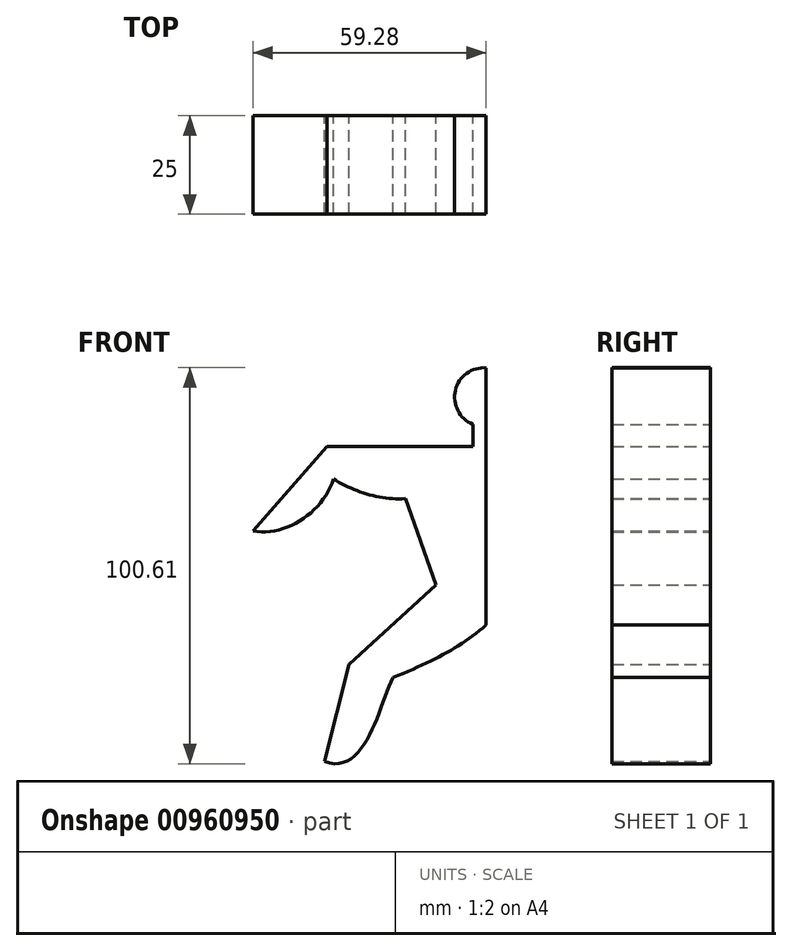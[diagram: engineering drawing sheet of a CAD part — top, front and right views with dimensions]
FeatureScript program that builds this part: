
annotation { "Feature Type Name" : "Feature", "Feature Type Description" : "" }
export const myFeature = defineFeature(function(context is Context, id is Id, definition is map)
    precondition{}
    {
        {
            var Q0;
            Q0=qCreatedBy(makeId("Front.planeOp"),FACE);
            var sketch = newSketch(context, id + "F0", { "sketchPlane" : qUnion([Q0])});
            skLineSegment(sketch, "E0", {"start": v(-3.4, 30.59) * mm, "end": v(-3.4, 24.97) * mm});
            skLineSegment(sketch, "E1", {"start": v(-3.4, 24.97) * mm, "end": v(-40.44, 24.97) * mm});
            skLineSegment(sketch, "E2", {"start": v(-40.44, 24.97) * mm, "end": v(-59.28, 3.51) * mm});
            skLineSegment(sketch, "E3", {"start": v(-20.5, 11.74) * mm, "end": v(-12.75, -10.25) * mm});
            skLineSegment(sketch, "E4", {"start": v(-12.75, -10.25) * mm, "end": v(-34.88, -30.44) * mm});
            skLineSegment(sketch, "E5", {"start": v(-34.88, -30.44) * mm, "end": v(-41.13, -55.05) * mm});
            skFitSpline(sketch, "E6", {"points": [v(-59.28, 3.51) * mm, v(-38.82, 16.7) * mm], "startDerivative": vector(24.73, -5.03) * mm, "endDerivative": vector(7.62, 25.02) * mm});
            skFitSpline(sketch, "E7", {"points": [v(-38.82, 16.7) * mm, v(-20.5, 11.74) * mm], "startDerivative": vector(16.19, -9.8) * mm, "endDerivative": vector(19.1, 1.69) * mm});
            skFitSpline(sketch, "E8", {"points": [v(-41.13, -55.05) * mm, v(-23.7, -33.74) * mm], "startDerivative": vector(31.12, -11.97) * mm, "endDerivative": vector(11.29, 24.28) * mm});
            skPoint(sketch, "E9.1.internal.snap0", {"position": v(-23.81, -20.35) * mm});
            skFitSpline(sketch, "E9", {"points": [v(-23.7, -33.74) * mm, v(0, -20.35) * mm], "startDerivative": vector(31.12, 12.31) * mm, "endDerivative": vector(20.12, 17.26) * mm});
            skArc(sketch, "E10", {"start": v(0, 44.95) * mm, "mid": v(-7.83, 39.22) * mm, "end": v(-3.4, 30.59) * mm});
            skLineSegment(sketch, "E11", {"start": v(0, 44.95) * mm, "end": v(0, -21.96) * mm, "construction": true});
            skLineSegment(sketch, "E12.MirrorCS", {"start": v(20.5, 11.74) * mm, "end": v(12.75, -10.25) * mm});
            skLineSegment(sketch, "E13.MirrorCS", {"start": v(34.88, -30.44) * mm, "end": v(41.13, -55.05) * mm});
            skLineSegment(sketch, "E14.MirrorCS", {"start": v(40.44, 24.97) * mm, "end": v(59.28, 3.51) * mm});
            skLineSegment(sketch, "E15.MirrorCS", {"start": v(3.4, 30.59) * mm, "end": v(3.4, 24.97) * mm});
            skLineSegment(sketch, "E16.MirrorCS", {"start": v(12.75, -10.25) * mm, "end": v(34.88, -30.44) * mm});
            skFitSpline(sketch, "E17.MirrorCS", {"points": [v(59.28, 3.51) * mm, v(38.82, 16.7) * mm], "startDerivative": vector(-24.73, -5.03) * mm, "endDerivative": vector(-7.62, 25.02) * mm});
            skFitSpline(sketch, "E18.MirrorCS", {"points": [v(41.13, -55.05) * mm, v(23.7, -33.74) * mm], "startDerivative": vector(-31.12, -11.97) * mm, "endDerivative": vector(-11.29, 24.28) * mm});
            skLineSegment(sketch, "E19.MirrorCS", {"start": v(3.4, 24.97) * mm, "end": v(40.44, 24.97) * mm});
            skFitSpline(sketch, "E20.MirrorCS", {"points": [v(38.82, 16.7) * mm, v(20.5, 11.74) * mm], "startDerivative": vector(-16.19, -9.8) * mm, "endDerivative": vector(-19.1, 1.69) * mm});
            skPoint(sketch, "E21.MirrorP", {"position": v(23.81, -20.35) * mm});
            skArc(sketch, "E22.MirrorCS", {"start": v(0, 44.95) * mm, "mid": v(7.83, 39.22) * mm, "end": v(3.4, 30.59) * mm});
            skFitSpline(sketch, "E23.MirrorCS", {"points": [v(23.7, -33.74) * mm, v(0, -20.35) * mm], "startDerivative": vector(-31.12, 12.31) * mm, "endDerivative": vector(-20.12, 17.26) * mm});
            skLineSegment(sketch, "E24", {"start": v(0, 44.95) * mm, "end": v(0, -20.35) * mm});
            skSolve(sketch);
        }
        {
            var Q0;
            Q0=makeQuery(id+"F0.imprint","IMPRINT",FACE,{"disambiguationData":[TD([[makeQuery(id+"F0.imprint","IMPRINT",EDGE,{"derivedFrom":sQuery(id+"F0.wireOp",EDGE,"E0")}),1.0]])]});
            extrude(context, id + "F1", {"entities" : qUnion([Q0]), "depth" : 25 * mm, "offsetDistance" : 25 * mm});
        }
    });
